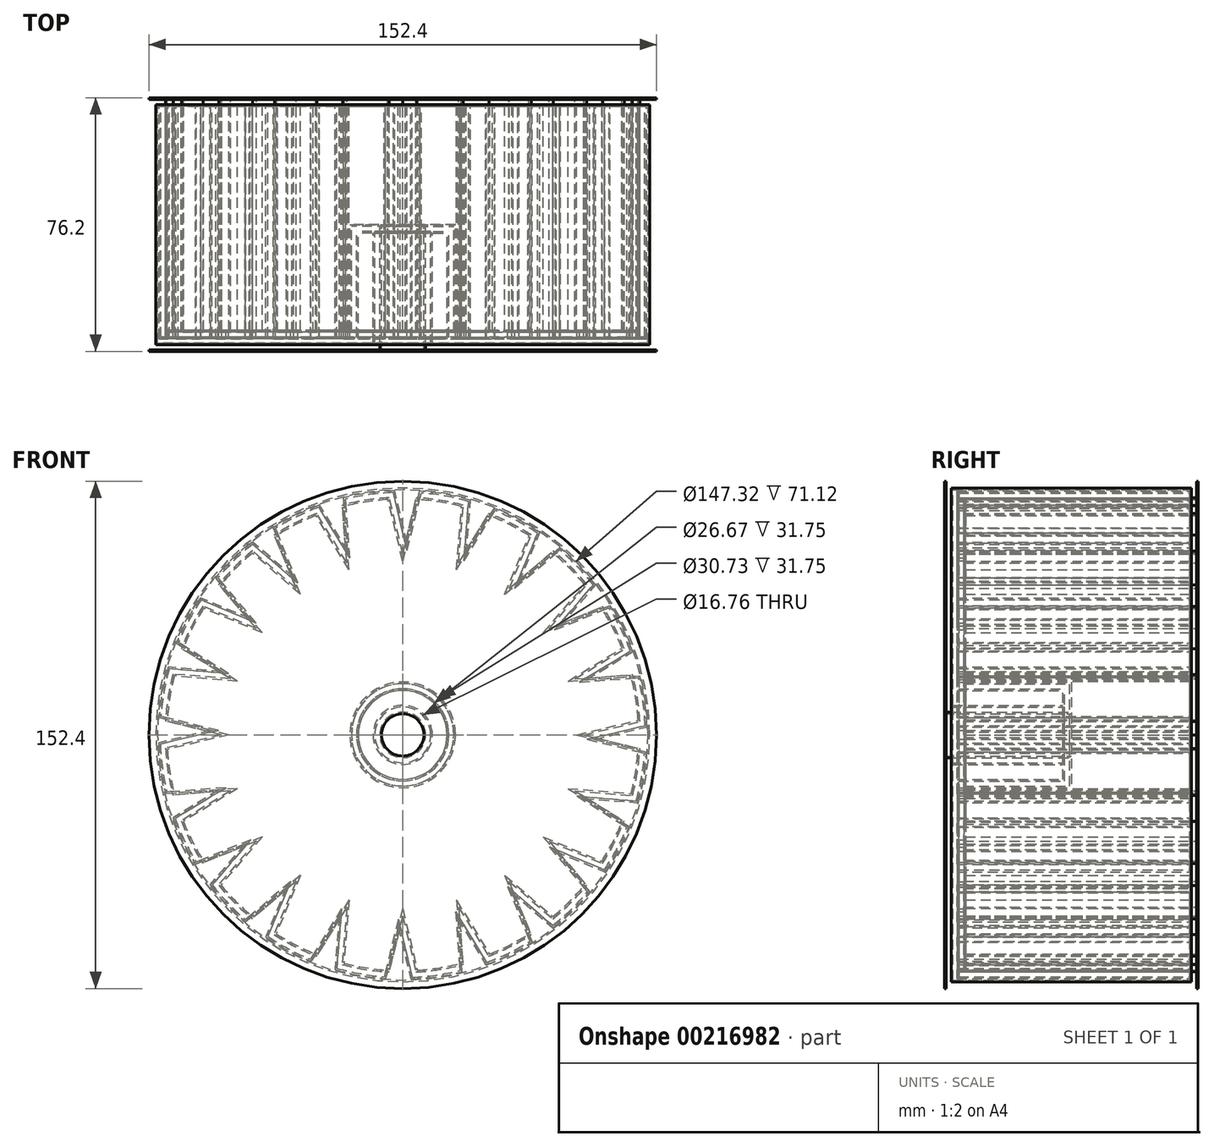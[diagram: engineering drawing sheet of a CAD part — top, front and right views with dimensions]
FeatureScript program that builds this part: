
annotation { "Feature Type Name" : "Feature", "Feature Type Description" : "" }
export const myFeature = defineFeature(function(context is Context, id is Id, definition is map)
    precondition{}
    {
        {
            var Q0;
            Q0=qCreatedBy(makeId("Front.planeOp"),FACE);
            var sketch = newSketch(context, id + "F0", { "sketchPlane" : qUnion([Q0])});
            skCircle(sketch, "E0", {"center": v(0, 0) * mm, "radius": 76.2 * mm});
            skSolve(sketch);
        }
        {
            var Q0;
            Q0=makeQuery(id+"F0.imprint","IMPRINT",FACE,{"disambiguationData":[TD([[makeQuery(id+"F0.imprint","IMPRINT",EDGE,{"derivedFrom":sQuery(id+"F0.wireOp",EDGE,"E0")}),1.0]])]});
            extrude(context, id + "F1", {"entities" : qUnion([Q0]), "depth" : 76.2 * mm});
        }
        {
            var Q0;
            Q0=makeQuery(id+"F1.opExtrude","CAP_FACE",FACE,{"disambiguationData":[OSD([sQuery(id+"F0.wireOp",EDGE,"E0")])],"isStart":true});
            var sketch = newSketch(context, id + "F2", { "sketchPlane" : qUnion([Q0])});
            skCircle(sketch, "E1", {"center": v(0, 0) * mm, "radius": 70.83 * mm});
            skCircle(sketch, "E2", {"center": v(0, 0) * mm, "radius": 15.88 * mm});
            skCircle(sketch, "E3", {"center": v(0, 0) * mm, "radius": 6.35 * mm});
            skLineSegment(sketch, "E4", {"start": v(0, 52.18) * mm, "end": v(4.39, 70.7) * mm});
            skLineSegment(sketch, "E5", {"start": v(0, 52.18) * mm, "end": v(-4.54, 70.68) * mm});
            skPoint(sketch, "E6.start.orphan", {"position": v(0, 70.83) * mm});
            skLineSegment(sketch, "E7.1.0", {"start": v(-16.12, 49.63) * mm, "end": v(-26.16, 65.82) * mm});
            skLineSegment(sketch, "E7.1.1", {"start": v(-16.12, 49.63) * mm, "end": v(-17.67, 68.59) * mm});
            skLineSegment(sketch, "E7.2.0", {"start": v(-30.67, 42.21) * mm, "end": v(-45.22, 54.52) * mm});
            skLineSegment(sketch, "E7.2.1", {"start": v(-30.67, 42.21) * mm, "end": v(-38, 59.77) * mm});
            skLineSegment(sketch, "E7.3.0", {"start": v(-42.21, 30.67) * mm, "end": v(-59.85, 37.88) * mm});
            skLineSegment(sketch, "E7.3.1", {"start": v(-42.21, 30.67) * mm, "end": v(-54.61, 45.1) * mm});
            skLineSegment(sketch, "E7.4.0", {"start": v(-49.63, 16.12) * mm, "end": v(-68.62, 17.53) * mm});
            skLineSegment(sketch, "E7.4.1", {"start": v(-49.63, 16.12) * mm, "end": v(-65.88, 26.02) * mm});
            skLineSegment(sketch, "E7.5.0", {"start": v(-52.18, 0) * mm, "end": v(-70.68, -4.54) * mm});
            skLineSegment(sketch, "E7.5.1", {"start": v(-52.18, 0) * mm, "end": v(-70.7, 4.39) * mm});
            skLineSegment(sketch, "E7.6.0", {"start": v(-49.63, -16.12) * mm, "end": v(-65.82, -26.16) * mm});
            skLineSegment(sketch, "E7.6.1", {"start": v(-49.63, -16.12) * mm, "end": v(-68.59, -17.67) * mm});
            skLineSegment(sketch, "E7.7.0", {"start": v(-42.21, -30.67) * mm, "end": v(-54.52, -45.22) * mm});
            skLineSegment(sketch, "E7.7.1", {"start": v(-42.21, -30.67) * mm, "end": v(-59.77, -38) * mm});
            skLineSegment(sketch, "E7.8.0", {"start": v(-30.67, -42.21) * mm, "end": v(-37.88, -59.85) * mm});
            skLineSegment(sketch, "E7.8.1", {"start": v(-30.67, -42.21) * mm, "end": v(-45.1, -54.61) * mm});
            skLineSegment(sketch, "E7.9.0", {"start": v(-16.12, -49.63) * mm, "end": v(-17.53, -68.62) * mm});
            skLineSegment(sketch, "E7.9.1", {"start": v(-16.12, -49.63) * mm, "end": v(-26.02, -65.88) * mm});
            skLineSegment(sketch, "E7.10.0", {"start": v(0, -52.18) * mm, "end": v(4.54, -70.68) * mm});
            skLineSegment(sketch, "E7.10.1", {"start": v(0, -52.18) * mm, "end": v(-4.39, -70.7) * mm});
            skLineSegment(sketch, "E7.11.0", {"start": v(16.12, -49.63) * mm, "end": v(26.16, -65.82) * mm});
            skLineSegment(sketch, "E7.11.1", {"start": v(16.12, -49.63) * mm, "end": v(17.67, -68.59) * mm});
            skLineSegment(sketch, "E7.12.0", {"start": v(30.67, -42.21) * mm, "end": v(45.22, -54.52) * mm});
            skLineSegment(sketch, "E7.12.1", {"start": v(30.67, -42.21) * mm, "end": v(38, -59.77) * mm});
            skLineSegment(sketch, "E7.13.0", {"start": v(42.21, -30.67) * mm, "end": v(59.85, -37.88) * mm});
            skLineSegment(sketch, "E7.13.1", {"start": v(42.21, -30.67) * mm, "end": v(54.61, -45.1) * mm});
            skLineSegment(sketch, "E7.14.0", {"start": v(49.63, -16.12) * mm, "end": v(68.62, -17.53) * mm});
            skLineSegment(sketch, "E7.14.1", {"start": v(49.63, -16.12) * mm, "end": v(65.88, -26.02) * mm});
            skLineSegment(sketch, "E7.15.0", {"start": v(52.18, 0) * mm, "end": v(70.68, 4.54) * mm});
            skLineSegment(sketch, "E7.15.1", {"start": v(52.18, 0) * mm, "end": v(70.7, -4.39) * mm});
            skLineSegment(sketch, "E7.16.0", {"start": v(49.63, 16.12) * mm, "end": v(65.82, 26.16) * mm});
            skLineSegment(sketch, "E7.16.1", {"start": v(49.63, 16.12) * mm, "end": v(68.59, 17.67) * mm});
            skLineSegment(sketch, "E7.17.0", {"start": v(42.21, 30.67) * mm, "end": v(54.52, 45.22) * mm});
            skLineSegment(sketch, "E7.17.1", {"start": v(42.21, 30.67) * mm, "end": v(59.77, 38) * mm});
            skLineSegment(sketch, "E7.18.0", {"start": v(30.67, 42.21) * mm, "end": v(37.88, 59.85) * mm});
            skLineSegment(sketch, "E7.18.1", {"start": v(30.67, 42.21) * mm, "end": v(45.1, 54.61) * mm});
            skLineSegment(sketch, "E7.19.0", {"start": v(16.12, 49.63) * mm, "end": v(17.53, 68.62) * mm});
            skLineSegment(sketch, "E7.19.1", {"start": v(16.12, 49.63) * mm, "end": v(26.02, 65.88) * mm});
            skSolve(sketch);
        }
        {
            var Q0;
            Q0=makeQuery(id+"F2.imprint","IMPRINT",FACE,{"disambiguationData":[TD([[makeQuery(id+"F2.imprint","IMPRINT",EDGE,{"derivedFrom":sQuery(id+"F2.wireOp",EDGE,"E2")}),-1.0]])]});
            extrude(context, id + "F3", {"entities" : qUnion([Q0]), "operationType" : NewBodyOperationType.REMOVE, "oppositeDirection" : true, "depth" : 69.85 * mm});
        }
        {
            var Q0;
            Q0=makeQuery(id+"F2.imprint","IMPRINT",FACE,{"disambiguationData":[TD([[makeQuery(id+"F2.imprint","IMPRINT",EDGE,{"derivedFrom":sQuery(id+"F2.wireOp",EDGE,"E3")}),1.0]])]});
            extrude(context, id + "F4", {"entities" : qUnion([Q0]), "operationType" : NewBodyOperationType.REMOVE, "endBound" : BoundingType.THROUGH_ALL, "oppositeDirection" : true, "depth" : 25.4 * mm});
        }
        {
            var Q0;
            Q0=makeQuery(id+"F3.boolean.opBoolean","SPLIT",FACE,{"disambiguationData":[TD([makeQuery(id+"F3.opExtrude","SWEPT_FACE",FACE,{"disambiguationData":[OSD([sQuery(id+"F2.wireOp",EDGE,"E2")])]})])],"derivedFrom":makeQuery(id+"F1.opExtrude","CAP_FACE",FACE,{"disambiguationData":[OSD([sQuery(id+"F0.wireOp",EDGE,"E0")])],"isStart":true})});
            extrude(context, id + "F5", {"entities" : qUnion([Q0]), "operationType" : NewBodyOperationType.REMOVE, "oppositeDirection" : true, "depth" : 38.1 * mm});
        }
        {
            var Q0;
            Q0=makeQuery(id+"F3.boolean.opBoolean","COPY",FACE,{"derivedFrom":makeQuery(id+"F3.opExtrude","SWEPT_FACE",FACE,{"disambiguationData":[OSD([sQuery(id+"F2.wireOp",EDGE,"E7.16.0")])]})});
            var Q1;
            Q1=makeQuery(id+"F3.boolean.opBoolean","COPY",FACE,{"derivedFrom":makeQuery(id+"F3.opExtrude","SWEPT_FACE",FACE,{"disambiguationData":[OSD([sQuery(id+"F2.wireOp",EDGE,"E7.15.0")])]})});
            var Q2;
            Q2=makeQuery(id+"F3.boolean.opBoolean","COPY",FACE,{"derivedFrom":makeQuery(id+"F3.opExtrude","SWEPT_FACE",FACE,{"disambiguationData":[OSD([sQuery(id+"F2.wireOp",EDGE,"E7.14.0")])]})});
            var Q3;
            Q3=makeQuery(id+"F3.boolean.opBoolean","COPY",FACE,{"derivedFrom":makeQuery(id+"F3.opExtrude","SWEPT_FACE",FACE,{"disambiguationData":[OSD([sQuery(id+"F2.wireOp",EDGE,"E7.13.0")])]})});
            var Q4;
            Q4=makeQuery(id+"F3.boolean.opBoolean","COPY",FACE,{"derivedFrom":makeQuery(id+"F3.opExtrude","SWEPT_FACE",FACE,{"disambiguationData":[OSD([sQuery(id+"F2.wireOp",EDGE,"E7.12.0")])]})});
            var Q5;
            Q5=makeQuery(id+"F3.boolean.opBoolean","COPY",FACE,{"derivedFrom":makeQuery(id+"F3.opExtrude","SWEPT_FACE",FACE,{"disambiguationData":[OSD([sQuery(id+"F2.wireOp",EDGE,"E7.11.0")])]})});
            var Q6;
            Q6=makeQuery(id+"F3.boolean.opBoolean","COPY",FACE,{"derivedFrom":makeQuery(id+"F3.opExtrude","SWEPT_FACE",FACE,{"disambiguationData":[OSD([sQuery(id+"F2.wireOp",EDGE,"E7.10.0")])]})});
            var Q7;
            Q7=makeQuery(id+"F3.boolean.opBoolean","COPY",FACE,{"derivedFrom":makeQuery(id+"F3.opExtrude","SWEPT_FACE",FACE,{"disambiguationData":[OSD([sQuery(id+"F2.wireOp",EDGE,"E7.8.0")])]})});
            var Q8;
            Q8=makeQuery(id+"F3.boolean.opBoolean","COPY",FACE,{"derivedFrom":makeQuery(id+"F3.opExtrude","SWEPT_FACE",FACE,{"disambiguationData":[OSD([sQuery(id+"F2.wireOp",EDGE,"E7.9.0")])]})});
            var Q9;
            Q9=makeQuery(id+"F3.boolean.opBoolean","COPY",FACE,{"derivedFrom":makeQuery(id+"F3.opExtrude","SWEPT_FACE",FACE,{"disambiguationData":[OSD([sQuery(id+"F2.wireOp",EDGE,"E7.7.0")])]})});
            var Q10;
            Q10=makeQuery(id+"F3.boolean.opBoolean","COPY",FACE,{"derivedFrom":makeQuery(id+"F3.opExtrude","SWEPT_FACE",FACE,{"disambiguationData":[OSD([sQuery(id+"F2.wireOp",EDGE,"E7.6.0")])]})});
            var Q11;
            Q11=makeQuery(id+"F3.boolean.opBoolean","COPY",FACE,{"derivedFrom":makeQuery(id+"F3.opExtrude","SWEPT_FACE",FACE,{"disambiguationData":[OSD([sQuery(id+"F2.wireOp",EDGE,"E7.5.0")])]})});
            var Q12;
            Q12=makeQuery(id+"F3.boolean.opBoolean","COPY",FACE,{"derivedFrom":makeQuery(id+"F3.opExtrude","SWEPT_FACE",FACE,{"disambiguationData":[OSD([sQuery(id+"F2.wireOp",EDGE,"E7.4.0")])]})});
            var Q13;
            Q13=makeQuery(id+"F3.boolean.opBoolean","COPY",FACE,{"derivedFrom":makeQuery(id+"F3.opExtrude","SWEPT_FACE",FACE,{"disambiguationData":[OSD([sQuery(id+"F2.wireOp",EDGE,"E7.3.0")])]})});
            var Q14;
            Q14=makeQuery(id+"F3.boolean.opBoolean","COPY",FACE,{"derivedFrom":makeQuery(id+"F3.opExtrude","SWEPT_FACE",FACE,{"disambiguationData":[OSD([sQuery(id+"F2.wireOp",EDGE,"E7.2.0")])]})});
            var Q15;
            Q15=makeQuery(id+"F3.boolean.opBoolean","COPY",FACE,{"derivedFrom":makeQuery(id+"F3.opExtrude","SWEPT_FACE",FACE,{"disambiguationData":[OSD([sQuery(id+"F2.wireOp",EDGE,"E7.1.0")])]})});
            var Q16;
            Q16=makeQuery(id+"F3.boolean.opBoolean","COPY",FACE,{"derivedFrom":makeQuery(id+"F3.opExtrude","SWEPT_FACE",FACE,{"disambiguationData":[OSD([sQuery(id+"F2.wireOp",EDGE,"E5")])]})});
            var Q17;
            Q17=makeQuery(id+"F3.boolean.opBoolean","COPY",FACE,{"derivedFrom":makeQuery(id+"F3.opExtrude","SWEPT_FACE",FACE,{"disambiguationData":[OSD([sQuery(id+"F2.wireOp",EDGE,"E7.19.0")])]})});
            var Q18;
            Q18=makeQuery(id+"F3.boolean.opBoolean","COPY",FACE,{"derivedFrom":makeQuery(id+"F3.opExtrude","SWEPT_FACE",FACE,{"disambiguationData":[OSD([sQuery(id+"F2.wireOp",EDGE,"E7.18.0")])]})});
            var Q19;
            Q19=makeQuery(id+"F3.boolean.opBoolean","COPY",FACE,{"derivedFrom":makeQuery(id+"F3.opExtrude","SWEPT_FACE",FACE,{"disambiguationData":[OSD([sQuery(id+"F2.wireOp",EDGE,"E7.17.0")])]})});
            shell(context, id + "F6", {"entities" : qUnion([Q0, Q1, Q2, Q3, Q4, Q5, Q6, Q7, Q8, Q9, Q10, Q11, Q12, Q13, Q14, Q15, Q16, Q17, Q18, Q19]), "thickness" : 2.54 * mm});
        }
        {
            var Q0;
            Q0=makeQuery(id+"F1.opExtrude","SWEPT_FACE",FACE,{"disambiguationData":[OSD([sQuery(id+"F0.wireOp",EDGE,"E0")])]});
            shell(context, id + "F7", {"entities" : qUnion([Q0]), "thickness" : 0.5 * mm});
        }
    });
